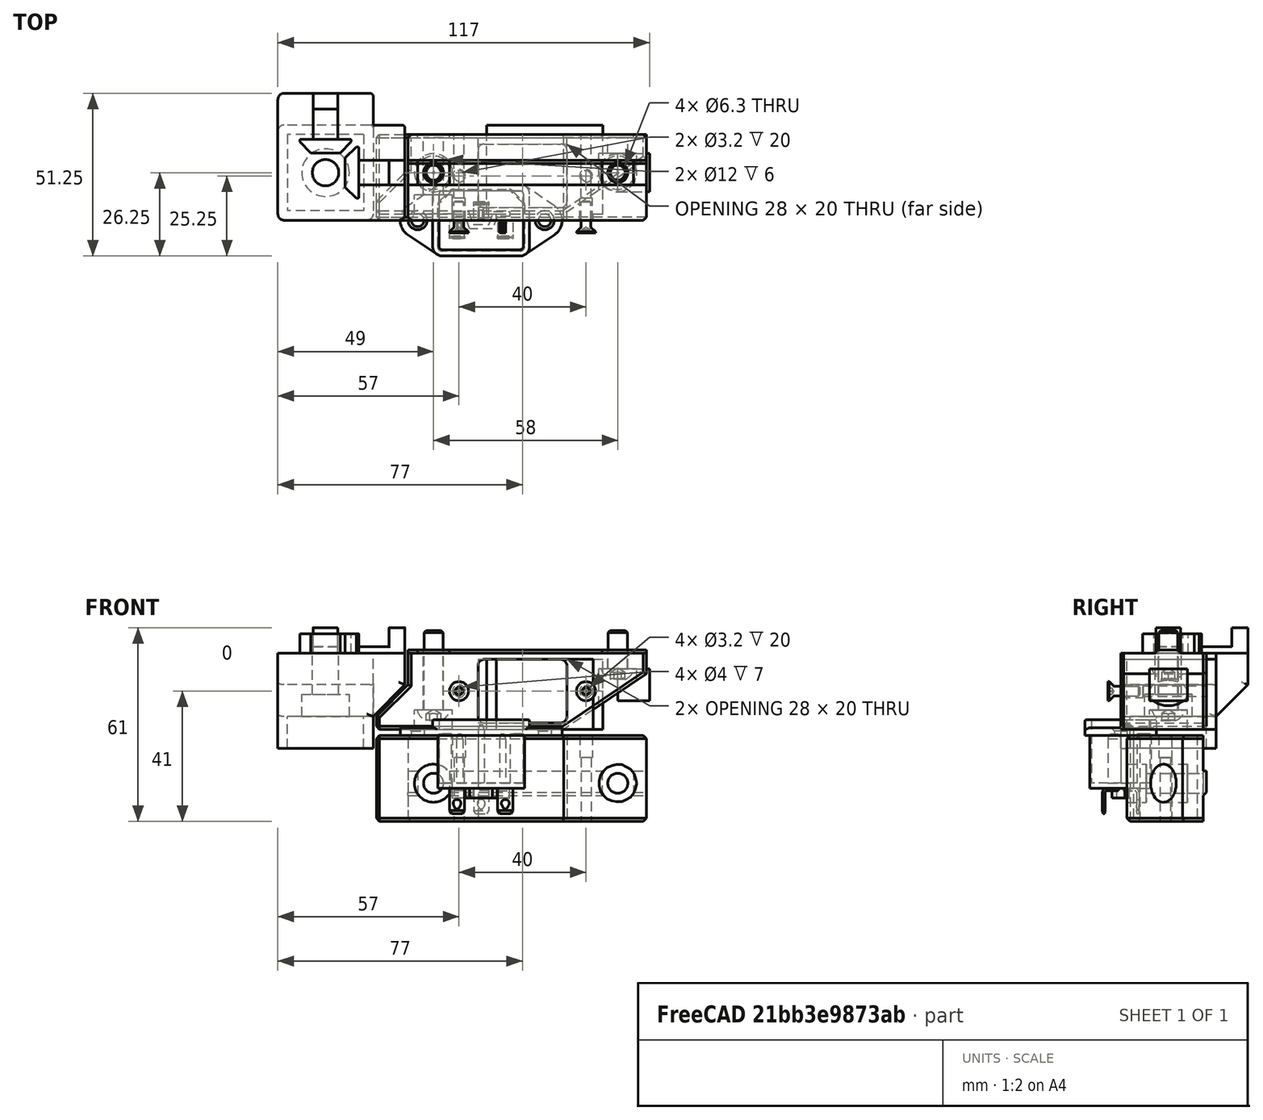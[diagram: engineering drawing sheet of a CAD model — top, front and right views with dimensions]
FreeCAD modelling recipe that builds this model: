
FCSTD DOCUMENT  (FreeCAD 0.19R24291 (Git))
Label: ac-plug
License: Other
LicenseURL: GPL3
objects: Part::Box×9, Part::Cylinder×8, Part::MultiFuse×7, Part::Feature×7, Part::Chamfer×4, Part::FeaturePython×4, Part::Cut×3, App::Part×2, Part::Refine×2, Part::Fillet×1
note: 45 computed .brp shape members not serialized (recipe doc carries the construction recipe); baked Part::Feature solids carry a one-line shape summary decoded from their .brp

FEATURE [Part::Box] Box  label="Cube"
  AttacherType = Attacher::AttachEngine3D
  Height = 20
  Length = 28
  Placement = pos=(-14,0,7) rot=(0,0,1;0rad)
  Width = 30
FEATURE [Part::Cylinder] Cylinder
  Angle = 360
  AttacherType = Attacher::AttachEngine3D
  Height = 7
  Placement = pos=(-20,4e-15,17) rot=(-1,0,0;1.5708rad)
  Radius = 2
FEATURE [Part::Cylinder] Cylinder001
  Angle = 360
  AttacherType = Attacher::AttachEngine3D
  Height = 7
  Placement = pos=(20,4e-15,17) rot=(-1,0,0;1.5708rad)
  Radius = 2
FEATURE [Part::Cylinder] Cylinder002
  Angle = 360
  AttacherType = Attacher::AttachEngine3D
  Height = 30
  Placement = pos=(20,4e-15,17) rot=(-1,0,0;1.5708rad)
  Radius = 1.6
FEATURE [Part::Cylinder] Cylinder003
  Angle = 360
  AttacherType = Attacher::AttachEngine3D
  Height = 30
  Placement = pos=(-20,4e-15,17) rot=(-1,0,0;1.5708rad)
  Radius = 1.6
FEATURE [Part::Fillet] Fillet
  Base = -> Box
  Edges = 4 edges r=2: [Edge2,Edge4,Edge6,Edge8]
FEATURE [Part::MultiFuse] Fusion  label="plug-slot"
  Placement = pos=(13,0,-3) rot=(0,0,1;0rad)
  Shapes = -> [Fillet,Cylinder003,Cylinder002,Cylinder001,Cylinder]
FEATURE [Part::Box] Box001  label="Cube001"
  AttacherType = Attacher::AttachEngine3D
  Height = 22
  Length = 30.5
  Width = 30
FEATURE [Part::Box] Box002  label="Cube002"
  AttacherType = Attacher::AttachEngine3D
  Height = 22
  Length = 36.5
  Placement = pos=(-3,2,0) rot=(0,0,1;0rad)
  Width = 28
FEATURE [Part::MultiFuse] Fusion001  label="switch-slot"
  Placement = pos=(4.75,0,2) rot=(0,0,1;0rad)
  Shapes = -> [Box002,Box001]
FEATURE [Part::Cylinder] Cylinder004
  Angle = 360
  AttacherType = Attacher::AttachEngine3D
  Height = 8
  Placement = pos=(0,15,0) rot=(0,0,1;0rad)
  Radius = 6
FEATURE [Part::Cylinder] Cylinder005
  Angle = 360
  AttacherType = Attacher::AttachEngine3D
  Height = 30
  Placement = pos=(0,15,0) rot=(0,0,1;0rad)
  Radius = 3.15
FEATURE [Part::Feature] Cut008004003004014002002007  label="foot004"
  Placement = pos=(-49,15,-4) rot=(0,0,1;3.14159rad)
  shape: bbox 40.3 x 40.3 x 38.3 mm, 68 faces (baked)
FEATURE [Part::Box] Box004  label="Cube004"
  AttacherType = Attacher::AttachEngine3D
  Height = 14
  Length = 11
  Placement = pos=(-33,0,2) rot=(0,0,1;0rad)
  Width = 27
FEATURE [Part::Chamfer] Chamfer
  Base = -> Box004
  Edges = 1 edges r=10: [Edge2]
FEATURE [Part::Box] Box003  label="Cube003"
  AttacherType = Attacher::AttachEngine3D
  Height = 24
  Length = 75
  Placement = pos=(-23,0,2) rot=(0,0,1;0rad)
  Width = 27
FEATURE [Part::Box] Box005  label="Cube005"
  AttacherType = Attacher::AttachEngine3D
  Height = 2
  Length = 75
  Placement = pos=(-23,11.1,25) rot=(0,0,1;0rad)
  Width = 7.8
FEATURE [Part::Cylinder] Cylinder006
  Angle = 360
  AttacherType = Attacher::AttachEngine3D
  Height = 30
  Placement = pos=(43,15,0) rot=(0,0,1;0rad)
  Radius = 3.15
FEATURE [Part::Cylinder] Cylinder007
  Angle = 360
  AttacherType = Attacher::AttachEngine3D
  Height = 21
  Placement = pos=(43,15,0) rot=(0,0,1;0rad)
  Radius = 6
FEATURE [Part::Feature] Part__Feature003  label="IEC Screw Mount Plug Socket Male003"
  shape: bbox 4.8 x 5 x 8 mm, 23 faces (baked)
FEATURE [Part::Feature] Part__Feature  label="IEC Screw Mount Plug Socket Male"
  shape: bbox 51.91 x 22.99 x 24.6 mm, 108 faces (baked)
FEATURE [Part::Feature] Part__Feature002  label="IEC Screw Mount Plug Socket Male002"
  shape: bbox 4.8 x 5 x 8 mm, 23 faces (baked)
FEATURE [Part::Feature] Part__Feature001  label="IEC Screw Mount Plug Socket Male001"
  shape: bbox 4.8 x 5 x 8 mm, 23 faces (baked)
FEATURE [App::Part] IEC_Screw_Mount_Plug_Socket_Male  label="IEC Screw Mount Plug Socket Male004"
  Group = -> [Part__Feature,Part__Feature001,Part__Feature002,Part__Feature003]
  Origin = -> Origin
  Placement = pos=(13,-1,14) rot=(0,-0.707107,0.707107;3.14159rad)
FEATURE [Part::Box] Box006  label="Cube006"
  AttacherType = Attacher::AttachEngine3D
  Height = 10
  Length = 10
  Placement = pos=(43,9,11) rot=(0,0,1;0rad)
  Width = 12
FEATURE [Part::MultiFuse] Fusion002005
  Shapes = -> [Cylinder006,Cylinder007]
FEATURE [Part::Chamfer] Chamfer002
  Base = -> Box003
  Edges = 1 edges: [Edge8 r1=17.5 r2=26]
FEATURE [Part::Chamfer] Chamfer003
  Base = -> Box005
  Edges = 1 edges r=1: [Edge12]
FEATURE [Part::MultiFuse] Fusion002008
  Shapes = -> [Chamfer003,Chamfer002,Chamfer]
FEATURE [Part::MultiFuse] Fusion002009
  Placement = pos=(-15,0,0) rot=(0,0,1;0rad)
  Shapes = -> [Cylinder004,Cylinder005]
FEATURE [Part::MultiFuse] Fusion002010
  Shapes = -> [Fusion002005,Fusion002009]
FEATURE [Part::Cut] Cut
  Base = -> Fusion002008
  Tool = -> Fusion002010
FEATURE [Part::Cut] Cut008004003004014002002008
  Base = -> Cut
  Tool = -> Fusion
FEATURE [Part::Refine] Cut008004003004014002002008001
  Source = -> Cut008004003004014002002008
FEATURE [Part::Chamfer] Chamfer004
  Base = -> Cut008004003004014002002008001
  Edges = 13 edges r=1: [Edge35,Edge38,Edge39,Edge41,Edge42,Edge44,Edge45,Edge46,Edge47,Edge48,Edge49,Edge50,Edge87]
FEATURE [Part::Feature] Chamfer004001
  shape: bbox 85 x 27 x 25 mm, 48 faces (baked)
FEATURE [App::Part] Part  label="AC-plug"
  Group = -> [IEC_Screw_Mount_Plug_Socket_Male,Chamfer004001]
  Origin = -> Origin001
FEATURE [Part::FeaturePython] Screw  label="M6x25-Screw"  # Fasteners workbench fastener (typed FeaturePython)
  Placement = pos=(-15,15,8) rot=(1,0,0;3.14159rad)
  baseObject = -> Chamfer004001 [Edge59]
  diameter = 4
  invert = true
  length = 5
  lengthCustom = 25
  matchOuter = true
  offset = 0
  thread = false
  type = 39
FEATURE [Part::FeaturePython] Screw001  label="M6x12-Screw"  # Fasteners workbench fastener (typed FeaturePython)
  Placement = pos=(43,15,21) rot=(1,0,0;3.14159rad)
  baseObject = -> Chamfer004001 [Edge61]
  diameter = 4
  invert = true
  length = 1
  lengthCustom = 12
  matchOuter = true
  offset = 0
  thread = false
  type = 39
FEATURE [Part::FeaturePython] Screw002  label="M3x10-Screw"  # Fasteners workbench fastener (typed FeaturePython)
  Placement = pos=(33,-4,14) rot=(1,0,0;1.5708rad)
  baseObject = -> Chamfer004001 [Edge102]
  diameter = 1
  invert = true
  length = 1
  lengthCustom = 10
  matchOuter = true
  offset = 4
  thread = false
  type = 17
FEATURE [Part::FeaturePython] Screw003  label="M3x10-Screw001"  # Fasteners workbench fastener (typed FeaturePython)
  Placement = pos=(-7,-4,14) rot=(1,0,0;1.5708rad)
  baseObject = -> Chamfer004001 [Edge101]
  diameter = 1
  invert = true
  length = 1
  lengthCustom = 10
  matchOuter = true
  offset = 4
  thread = false
  type = 17
FEATURE [Part::Box] Box007  label="Cube007"
  AttacherType = Attacher::AttachEngine3D
  Height = 10
  Length = 10
  Placement = pos=(-20,10,26) rot=(0,0,1;0rad)
  Width = 10
FEATURE [Part::Box] Box008  label="Cube008"
  AttacherType = Attacher::AttachEngine3D
  Height = 10
  Length = 10
  Placement = pos=(38,10,26) rot=(0,0,1;0rad)
  Width = 10
FEATURE [Part::MultiFuse] Fusion002011
  Shapes = -> [Box008,Box007]
FEATURE [Part::Cut] Cut008004003004014002002008002
  Base = -> Chamfer004
  Tool = -> Fusion002011
FEATURE [Part::Refine] Cut008004003004014002002008002001
  Source = -> Cut008004003004014002002008002
FEATURE [Part::Feature] Cut008004003004014002002008002001001
  Placement = pos=(0,0,0) rot=(1,0,0;4.71239rad)
  shape: bbox 85 x 25 x 27 mm, 57 faces (baked)
